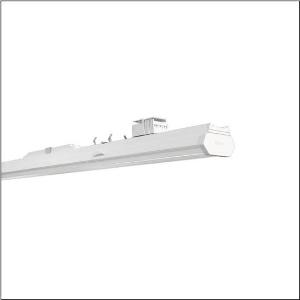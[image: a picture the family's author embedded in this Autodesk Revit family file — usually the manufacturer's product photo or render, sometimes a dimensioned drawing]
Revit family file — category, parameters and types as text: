
# Revit family: licross_11_protected_ho_51td12dn4fxm3s
name_source: partatom
category: Lighting Fixtures
units: mm (PartAtom-declared; Revit-internal decimal feet)

## family parameters
Cut with Voids When Loaded = No
Host = Face
Light Source = No
Part Type = Normal
Room Calculation Point = No
Round Connector Dimension = Use Diameter
Shared = No

## types (1)
- --- (1 x LED, 970 lm, 7.4 W, 4000K)
    Apparent Load = 7 VA
    CIE Flux Codes = 70 91 97 98 100
    Color Rendering = 80
    Color Temperature = 4000K
    Default Elevation = 1800 mm
    Description = Licross 11 Protected HO, luminaire insert, of sheet steel, galvanised, coil coated, white, length: 1.500mm, width: 90mm, height: 101mm, LED rated luminous flux: 15.270lm, light colour: 840, SDCM (Standard Deviation of Colour Matching)MacAdam ≤ 2 SDCM (initial), control gear: DALI 2 (for two DALI lines), with plug, 6-pole, with phase selection, for trunking rail, 14-core, mains connection: 220..240V, AC, 50/60Hz, rated input power: 91W, for trunking rail, 14-core, internal wiring halogen-free, for emergency light function, converter,control gear: single battery element, battery: LiFePO4, 9Ah, primary light control with lens, of plastic, primary optical cover: cover, of PMMA, light emission: direct distribution, primary light characteristic: symmetric, protection rating (complete): IP54, insulation class (complete): insulation class I (protective earthing), certification: CE, UKCA, protection symbol: D if used in an environment with non-conductive dust loads with corresponding accessories, impact resistance: IK06, permissible ambient temperature for indoor applications: +5..+30°C, standard: EN 60598-2-22, LABS conformity tested according to VDMA 24364:2018-05, reducing of maximum allowable ambient temperature of 5°C with ceiling mounting, corresponds to IFS (International Featured Standards) requirements for safety and quality in the food industry, The light source and the operating device comply with the requirements of the Ecodesign Regulation (EU) 2019/2020 and are replaceable in accordance with this regulation, packaging unit: 1 piece
    Height = 92 mm
    Lamp = 1 x LED
    Lamp Light Flux = 970 lm
    Lamp Power = 7.4 W
    Lamp count = 1
    Length = 1500 mm
    Luminous efficacy = 131 lm/W
    Manufacturer = Siteco
    ModVariant = No
    Model = 51TD12DN4FXM3S
    Mounting Place = Ceiling
    Mounting Type = Pendant
    Number of Poles = 1
    OnlyDefault = Yes
    Power Factor = 1
    Product Name = Licross 11 Protected HO
    Product group = luminaire insert | ceiling pendant
    ProductGroupID = 901
    Protection Class = Protection class I
    Protection Degree = IP 54
    RLX_Detail_Level = 1
    RLX_Emergency_Light_Flux = 0 lm
    RLX_Emergency_Type = 0
    RLX_Emergency_Type_DB = No
    RlxData = <blob elided: 25257 chars, md5=811ef5ac>
    Socket = socket
    Standby Power = 0 W
    System Light Flux = 970 lm
    System Power = 7 W
    Type Comments = : emergency light operation: 3 h
    Type Image = l_1256145.jpg
    URL = http://relux.com
    VarID = @adj_096433
    Voltage = 0 V
    Weight = 0.00 kg
    Width = 88 mm

## geometry (parser evidence)
native form markers: Blend x4, Sweep x10
no freeform markers — native parametric forms only
